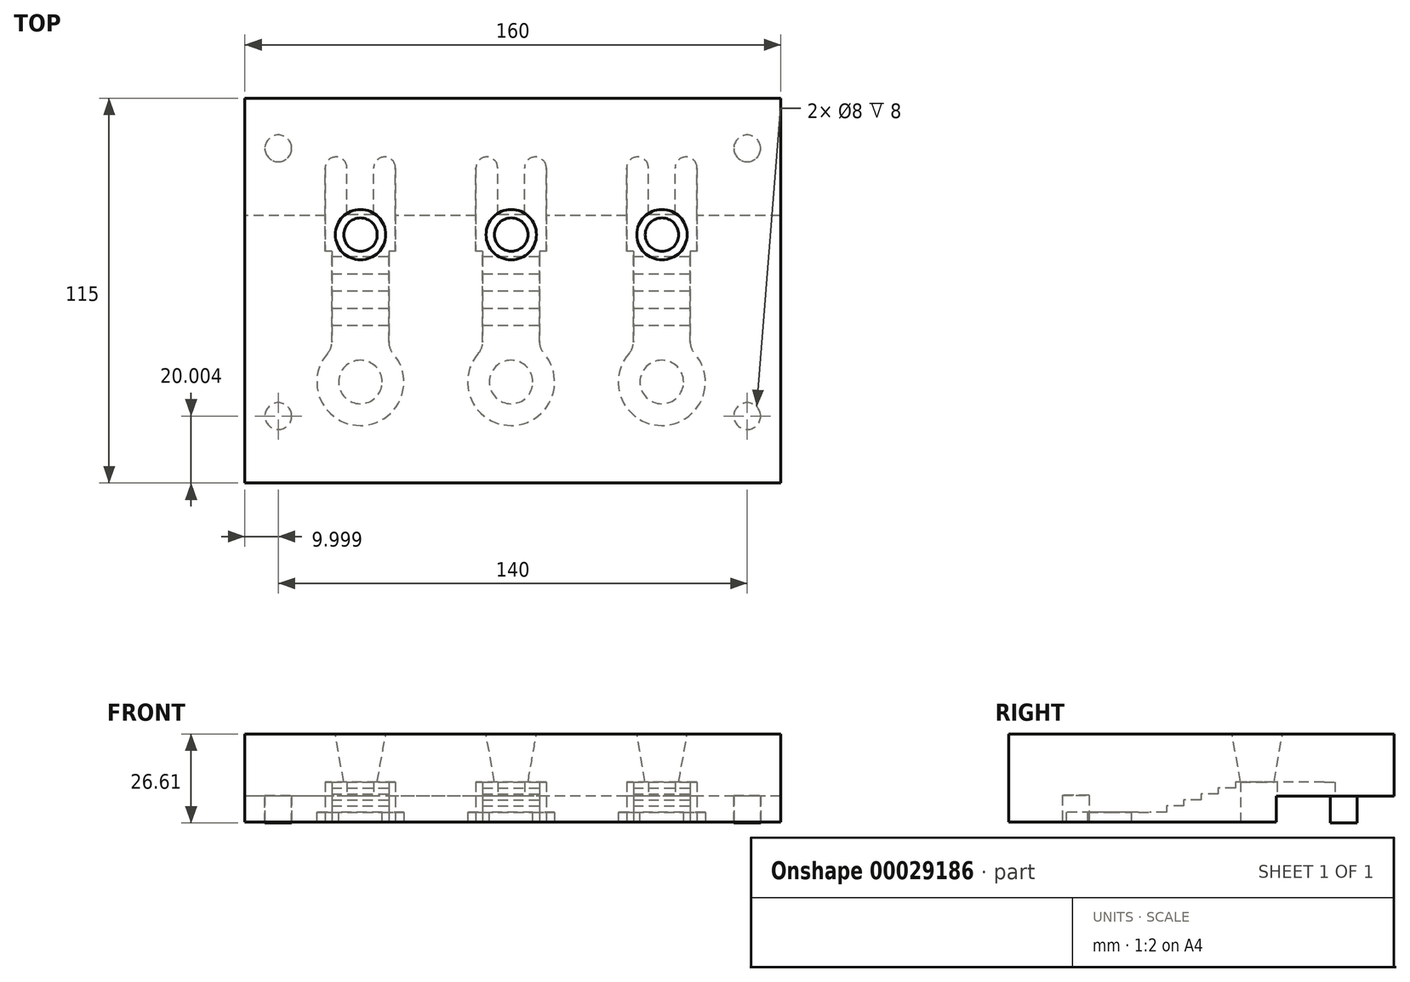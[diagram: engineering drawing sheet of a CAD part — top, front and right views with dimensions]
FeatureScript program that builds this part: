
annotation { "Feature Type Name" : "Feature", "Feature Type Description" : "" }
export const myFeature = defineFeature(function(context is Context, id is Id, definition is map)
    precondition{}
    {
        {
            var Q0;
            Q0=qCreatedBy(makeId("Top.planeOp"),FACE);
            var sketch = newSketch(context, id + "F0", { "sketchPlane" : qUnion([Q0])});
            skLineSegment(sketch, "E0.top", {"start": v(-85.13, 11.8) * mm, "end": v(-83.13, 11.8) * mm});
            skLineSegment(sketch, "E0.left", {"start": v(-85.13, 36.8) * mm, "end": v(-85.13, 11.8) * mm});
            skLineSegment(sketch, "E0.right", {"start": v(-64.13, 36.8) * mm, "end": v(-64.13, 11.8) * mm});
            skLineSegment(sketch, "E1.top", {"start": v(-78.63, 22.8) * mm, "end": v(-70.63, 22.8) * mm});
            skLineSegment(sketch, "E1.left", {"start": v(-78.63, 36.8) * mm, "end": v(-78.63, 22.8) * mm});
            skLineSegment(sketch, "E1.right", {"start": v(-70.63, 36.8) * mm, "end": v(-70.63, 22.8) * mm});
            skLineSegment(sketch, "E2.left", {"start": v(-83.13, 11.8) * mm, "end": v(-83.13, -15.3) * mm});
            skLineSegment(sketch, "E2.right", {"start": v(-66.13, 11.8) * mm, "end": v(-66.13, -15.3) * mm});
            skArc(sketch, "E3", {"start": v(-84.38, -18.6) * mm, "mid": v(-74.63, -40.2) * mm, "end": v(-64.88, -18.6) * mm});
            skLineSegment(sketch, "E4", {"start": v(-74.63, 22.8) * mm, "end": v(-74.63, -62.63) * mm, "construction": true});
            skPoint(sketch, "E5.visualSharp", {"position": v(-66.13, -17.37) * mm});
            skArc(sketch, "E5.filletArc", {"start": v(-66.13, -15.3) * mm, "mid": v(-65.8, -17.07) * mm, "end": v(-64.88, -18.6) * mm});
            skPoint(sketch, "E6.visualSharp", {"position": v(-83.13, -17.37) * mm});
            skArc(sketch, "E6.filletArc", {"start": v(-84.38, -18.6) * mm, "mid": v(-83.45, -17.07) * mm, "end": v(-83.13, -15.3) * mm});
            skPoint(sketch, "E7.visualSharp", {"position": v(-64.13, 11.8) * mm});
            skLineSegment(sketch, "E7.filletArc", {"start": v(-64.13, 11.8) * mm, "end": v(-64.13, 11.8) * mm});
            skPoint(sketch, "E8.visualSharp", {"position": v(-85.13, 11.8) * mm});
            skLineSegment(sketch, "E8.filletArc", {"start": v(-85.13, 11.8) * mm, "end": v(-85.13, 11.8) * mm});
            skLineSegment(sketch, "E9.trimOffspring", {"start": v(-66.13, 11.8) * mm, "end": v(-64.13, 11.8) * mm});
            skPoint(sketch, "E10.visualSharp", {"position": v(-83.13, 11.8) * mm});
            skLineSegment(sketch, "E10.filletArc", {"start": v(-83.13, 11.8) * mm, "end": v(-83.13, 11.8) * mm});
            skPoint(sketch, "E11.visualSharp", {"position": v(-66.13, 11.8) * mm});
            skLineSegment(sketch, "E11.filletArc", {"start": v(-66.13, 11.8) * mm, "end": v(-66.13, 11.8) * mm});
            skCircle(sketch, "E12", {"center": v(-74.63, -27.2) * mm, "radius": 6.5 * mm});
            skArc(sketch, "E13", {"start": v(-78.63, 36.8) * mm, "mid": v(-81.88, 40.05) * mm, "end": v(-85.13, 36.8) * mm});
            skArc(sketch, "E14", {"start": v(-64.13, 36.8) * mm, "mid": v(-67.38, 40.05) * mm, "end": v(-70.63, 36.8) * mm});
            skSolve(sketch);
        }
        {
            var Q0;
            Q0=makeQuery(id+"F0.imprint","IMPRINT",FACE,{"disambiguationData":[TD([[makeQuery(id+"F0.imprint","IMPRINT",EDGE,{"derivedFrom":sQuery(id+"F0.wireOp",EDGE,"E12")}),1.0]])]});
            var Q1;
            Q1=makeQuery(id+"F0.imprint","IMPRINT",FACE,{"disambiguationData":[TD([[makeQuery(id+"F0.imprint","IMPRINT",EDGE,{"derivedFrom":sQuery(id+"F0.wireOp",EDGE,"E0.top")}),1.0]])]});
            extrude(context, id + "F1", {"entities" : qUnion([Q0, Q1]), "depth" : 18 * mm});
        }
        {
            var Q0;
            Q0=qCreatedBy(makeId("Right.planeOp"),FACE);
            var sketch = newSketch(context, id + "F2", { "sketchPlane" : qUnion([Q0])});
            skLineSegment(sketch, "E15", {"start": v(-40.29, 25.83) * mm, "end": v(15.45, 25.83) * mm});
            skLineSegment(sketch, "E16", {"start": v(15.45, 25.83) * mm, "end": v(15.45, 18) * mm});
            skLineSegment(sketch, "E17", {"start": v(-10.3, 9) * mm, "end": v(-41.5, 9) * mm});
            skLineSegment(sketch, "E18", {"start": v(-41.5, 9) * mm, "end": v(-40.29, 25.83) * mm});
            skLineSegment(sketch, "E19", {"start": v(15.45, 18) * mm, "end": v(10.3, 18) * mm});
            skLineSegment(sketch, "E20", {"start": v(10.3, 18) * mm, "end": v(10.3, 16.2) * mm});
            skLineSegment(sketch, "E21", {"start": v(10.3, 16.2) * mm, "end": v(5.15, 16.2) * mm});
            skLineSegment(sketch, "E22", {"start": v(5.15, 16.2) * mm, "end": v(5.15, 14.4) * mm});
            skLineSegment(sketch, "E23", {"start": v(5.15, 14.4) * mm, "end": v(0, 14.4) * mm});
            skLineSegment(sketch, "E24", {"start": v(0, 14.4) * mm, "end": v(0, 12.6) * mm});
            skLineSegment(sketch, "E25", {"start": v(0, 12.6) * mm, "end": v(-5.15, 12.6) * mm});
            skLineSegment(sketch, "E26", {"start": v(-5.15, 12.6) * mm, "end": v(-5.15, 10.8) * mm});
            skLineSegment(sketch, "E27", {"start": v(-5.15, 10.8) * mm, "end": v(-10.3, 10.8) * mm});
            skLineSegment(sketch, "E28", {"start": v(-10.3, 10.8) * mm, "end": v(-10.3, 9) * mm});
            skSolve(sketch);
        }
        {
            var Q0;
            Q0=qSketchRegion(id+"F2",true);
            extrude(context, id + "F3", {"entities" : qUnion([Q0]), "operationType" : NewBodyOperationType.REMOVE, "oppositeDirection" : true, "depth" : 125 * mm});
        }
        {
            var Q0;
            Q0=makeQuery(id+"F3.boolean.opBoolean","COPY",FACE,{"derivedFrom":makeQuery(id+"F3.opExtrude","SWEPT_FACE",FACE,{"disambiguationData":[OSD([sQuery(id+"F2.wireOp",EDGE,"E17")])]})});
            var sketch = newSketch(context, id + "F4", { "sketchPlane" : qUnion([Q0])});
            skCircle(sketch, "E29", {"center": v(-74.63, -27.2) * mm, "radius": 6.5 * mm});
            skSolve(sketch);
        }
        {
            var Q0;
            Q0=qSketchRegion(id+"F4",true);
            extrude(context, id + "F5", {"entities" : qUnion([Q0]), "operationType" : NewBodyOperationType.REMOVE, "oppositeDirection" : true, "depth" : 3 * mm});
        }
        {
            var Q0;
            Q0=makeQuery(id+"F1.opExtrude","SWEPT_FACE",FACE,{"disambiguationData":[OSD([sQuery(id+"F0.wireOp",EDGE,"E0.right")])]});
            var sketch = newSketch(context, id + "F6", { "sketchPlane" : qUnion([Q0])});
            skCircle(sketch, "E30", {"center": v(30.8, 6) * mm, "radius": 2.5 * mm});
            skSolve(sketch);
        }
        {
            var Q0;
            Q0=makeQuery(id+"F1.opExtrude","SWEPT_FACE",FACE,{"disambiguationData":[OSD([sQuery(id+"F0.wireOp",EDGE,"E0.right")])]});
            var sketch = newSketch(context, id + "F7", { "sketchPlane" : qUnion([Q0])});
            skLineSegment(sketch, "E31", {"start": v(22.77, 0) * mm, "end": v(12.77, 0) * mm, "construction": true});
            skLineSegment(sketch, "E32", {"start": v(22.77, 0) * mm, "end": v(22.77, 17.98) * mm, "construction": true});
            skLineSegment(sketch, "E33", {"start": v(22.77, 17.98) * mm, "end": v(15.77, 17.98) * mm, "construction": true});
            skLineSegment(sketch, "E34", {"start": v(9.68, 20.3) * mm, "end": v(9.22, -2.99) * mm});
            skLineSegment(sketch, "E35", {"start": v(9.22, -2.99) * mm, "end": v(12.1, -2.99) * mm});
            skLineSegment(sketch, "E36", {"start": v(12.1, -2.99) * mm, "end": v(12.77, 0) * mm});
            skLineSegment(sketch, "E37", {"start": v(9.68, 20.3) * mm, "end": v(16.08, 19.87) * mm});
            skLineSegment(sketch, "E38", {"start": v(12.77, 0) * mm, "end": v(16.08, 19.87) * mm});
            skSolve(sketch);
        }
        {
            var Q0;
            Q0=makeQuery(id+"F1.opExtrude","SWEPT_FACE",FACE,{"disambiguationData":[OSD([sQuery(id+"F0.wireOp",EDGE,"E0.left")])]});
            var sketch = newSketch(context, id + "F8", { "sketchPlane" : qUnion([Q0])});
            skLineSegment(sketch, "E39", {"start": v(-12.8, 0) * mm, "end": v(-15.71, 18) * mm});
            skLineSegment(sketch, "E40", {"start": v(-15.71, 18) * mm, "end": v(-12.42, 21.29) * mm});
            skLineSegment(sketch, "E41", {"start": v(-12.42, 21.29) * mm, "end": v(-9.36, 20.22) * mm});
            skLineSegment(sketch, "E42", {"start": v(-9.36, 20.22) * mm, "end": v(-8.88, -2.86) * mm});
            skLineSegment(sketch, "E43", {"start": v(-8.88, -2.86) * mm, "end": v(-12.32, -2.93) * mm});
            skLineSegment(sketch, "E44", {"start": v(-12.32, -2.93) * mm, "end": v(-12.8, 0) * mm});
            skSolve(sketch);
        }
        {
            var Q0;
            Q0=makeQuery(id+"F1.opExtrude","SWEPT_FACE",FACE,{"disambiguationData":[OSD([sQuery(id+"F0.wireOp",EDGE,"E0.right")])]});
            var sketch = newSketch(context, id + "F9", { "sketchPlane" : qUnion([Q0])});
            skLineSegment(sketch, "E45", {"start": v(-57.39, 6) * mm, "end": v(-57.39, 32.33) * mm});
            skLineSegment(sketch, "E46", {"start": v(-57.39, 32.33) * mm, "end": v(57.61, 32.33) * mm});
            skLineSegment(sketch, "E47", {"start": v(57.61, 32.33) * mm, "end": v(57.61, 13.72) * mm});
            skLineSegment(sketch, "E48", {"start": v(57.61, 13.72) * mm, "end": v(57.61, -16.86) * mm});
            skLineSegment(sketch, "E49", {"start": v(57.61, -16.86) * mm, "end": v(-57.39, -16.86) * mm});
            skLineSegment(sketch, "E50", {"start": v(-57.39, -16.86) * mm, "end": v(-57.39, 6) * mm});
            skLineSegment(sketch, "E51", {"start": v(-57.39, 6) * mm, "end": v(22.49, 6) * mm});
            skLineSegment(sketch, "E52", {"start": v(22.49, 13.72) * mm, "end": v(22.49, 6) * mm});
            skLineSegment(sketch, "E53", {"start": v(22.49, 13.72) * mm, "end": v(57.61, 13.72) * mm});
            skSolve(sketch);
        }
        {
            var Q0;
            Q0=makeQuery(id+"F1.opExtrude","CAP_FACE",FACE,{"disambiguationData":[OSD([sQuery(id+"F0.wireOp",EDGE,"E0.top"),sQuery(id+"F0.wireOp",EDGE,"E0.left"),sQuery(id+"F0.wireOp",EDGE,"E0.right"),sQuery(id+"F0.wireOp",EDGE,"E1.top"),sQuery(id+"F0.wireOp",EDGE,"E1.left"),sQuery(id+"F0.wireOp",EDGE,"E1.right"),sQuery(id+"F0.wireOp",EDGE,"E2.left"),sQuery(id+"F0.wireOp",EDGE,"E2.right"),sQuery(id+"F0.wireOp",EDGE,"E3"),sQuery(id+"F0.wireOp",EDGE,"E5.filletArc"),sQuery(id+"F0.wireOp",EDGE,"E6.filletArc"),sQuery(id+"F0.wireOp",EDGE,"E9.trimOffspring"),sQuery(id+"F0.wireOp",EDGE,"E13"),sQuery(id+"F0.wireOp",EDGE,"E14")])],"isStart":false});
            var sketch = newSketch(context, id + "F10", { "sketchPlane" : qUnion([Q0])});
            skCircle(sketch, "E54", {"center": v(-74.58, 16.83) * mm, "radius": 5 * mm});
            skSolve(sketch);
        }
        {
            var Q0;
            Q0=qSketchRegion(id+"F10",true);
            extrude(context, id + "F11", {"entities" : qUnion([Q0]), "operationType" : NewBodyOperationType.ADD, "depth" : 25 * mm, "hasDraft" : true, "draftAngle" : 10 * degree});
        }
        {
            var Q0;
            {var subQ8=sQuery(id+"F9.wireOp",EDGE,"E52");Q0=makeQuery(id+"F9.imprint","IMPRINT",FACE,{"disambiguationData":[TD([[makeQuery(id+"F9.imprint","IMPRINT",EDGE,{"derivedFrom":subQ8}),-1.0]])]});}
            var Q1;
            {var subQ9=sQuery(id+"F9.wireOp",EDGE,"E45");Q1=makeQuery(id+"F9.imprint","IMPRINT",FACE,{"disambiguationData":[TD([[makeQuery(id+"F9.imprint","IMPRINT",EDGE,{"derivedFrom":subQ9}),-1.0]])]});}
            extrude(context, id + "F12", {"entities" : qUnion([Q0, Q1]), "depth" : 70 * mm, "hasSecondDirection" : true, "secondDirectionOppositeDirection" : true, "secondDirectionDepth" : 90 * mm});
        }
        {
            var Q0;
            Q0=makeQuery(id+"F12.opExtrude","SWEPT_FACE",FACE,{"disambiguationData":[OSD([sQuery(id+"F9.wireOp",EDGE,"E51")])]});
            var sketch = newSketch(context, id + "F13", { "sketchPlane" : qUnion([Q0])});
            skCircle(sketch, "E55", {"center": v(-144.13, 37.39) * mm, "radius": 4 * mm});
            skCircle(sketch, "E56", {"center": v(-4.13, 37.39) * mm, "radius": 4 * mm});
            skLineSegment(sketch, "E57", {"start": v(-144.13, 37.39) * mm, "end": v(-4.13, 37.39) * mm, "construction": true});
            skSolve(sketch);
        }
        {
            var Q0;
            Q0=makeQuery(id+"F12.opExtrude","SWEPT_FACE",FACE,{"disambiguationData":[OSD([sQuery(id+"F9.wireOp",EDGE,"E53")])]});
            var sketch = newSketch(context, id + "F14", { "sketchPlane" : qUnion([Q0])});
            skCircle(sketch, "E58", {"center": v(-144.13, -42.61) * mm, "radius": 4 * mm});
            skCircle(sketch, "E59", {"center": v(-4.13, -42.61) * mm, "radius": 4 * mm});
            skLineSegment(sketch, "E60", {"start": v(-144.13, -42.61) * mm, "end": v(-4.13, -42.61) * mm, "construction": true});
            skSolve(sketch);
        }
        {
            var Q0;
            Q0=makeQuery(id+"F14.imprint","IMPRINT",FACE,{"disambiguationData":[TD([[makeQuery(id+"F14.imprint","IMPRINT",EDGE,{"derivedFrom":sQuery(id+"F14.wireOp",EDGE,"E58")}),1.0]])]});
            var Q1;
            Q1=makeQuery(id+"F14.imprint","IMPRINT",FACE,{"disambiguationData":[TD([[makeQuery(id+"F14.imprint","IMPRINT",EDGE,{"derivedFrom":sQuery(id+"F14.wireOp",EDGE,"E59")}),1.0]])]});
            extrude(context, id + "F15", {"entities" : qUnion([Q0, Q1]), "operationType" : NewBodyOperationType.ADD, "depth" : 8 * mm});
        }
        {
            var Q0;
            Q0=makeQuery(id+"F13.imprint","IMPRINT",FACE,{"disambiguationData":[TD([[makeQuery(id+"F13.imprint","IMPRINT",EDGE,{"derivedFrom":sQuery(id+"F13.wireOp",EDGE,"E55")}),1.0]])]});
            var Q1;
            Q1=makeQuery(id+"F13.imprint","IMPRINT",FACE,{"disambiguationData":[TD([[makeQuery(id+"F13.imprint","IMPRINT",EDGE,{"derivedFrom":sQuery(id+"F13.wireOp",EDGE,"E56")}),1.0]])]});
            extrude(context, id + "F16", {"entities" : qUnion([Q0, Q1]), "operationType" : NewBodyOperationType.REMOVE, "oppositeDirection" : true, "depth" : 8 * mm});
        }
        {
            var Q0;
            Q0=makeQuery(id+"F1.opExtrude","SWEPT_BODY",BODY,{"disambiguationData":[OSD([sQuery(id+"F0.wireOp",EDGE,"E0.top"),sQuery(id+"F0.wireOp",EDGE,"E0.left"),sQuery(id+"F0.wireOp",EDGE,"E0.right"),sQuery(id+"F0.wireOp",EDGE,"E1.top"),sQuery(id+"F0.wireOp",EDGE,"E1.left"),sQuery(id+"F0.wireOp",EDGE,"E1.right"),sQuery(id+"F0.wireOp",EDGE,"E2.left"),sQuery(id+"F0.wireOp",EDGE,"E2.right"),sQuery(id+"F0.wireOp",EDGE,"E3"),sQuery(id+"F0.wireOp",EDGE,"E5.filletArc"),sQuery(id+"F0.wireOp",EDGE,"E6.filletArc"),sQuery(id+"F0.wireOp",EDGE,"E9.trimOffspring"),sQuery(id+"F0.wireOp",EDGE,"E13"),sQuery(id+"F0.wireOp",EDGE,"E14")])]});
            transform(context, id + "F17", {"entities" : qUnion([Q0]), "transformType" : TransformType.TRANSLATION_3D, "dx" : 45 * mm, "dy" : 0 * mm, "dz" : 0 * mm, "makeCopy" : true});
        }
        {
            var Q0;
            Q0=makeQuery(id+"F1.opExtrude","SWEPT_BODY",BODY,{"disambiguationData":[OSD([sQuery(id+"F0.wireOp",EDGE,"E0.top"),sQuery(id+"F0.wireOp",EDGE,"E0.left"),sQuery(id+"F0.wireOp",EDGE,"E0.right"),sQuery(id+"F0.wireOp",EDGE,"E1.top"),sQuery(id+"F0.wireOp",EDGE,"E1.left"),sQuery(id+"F0.wireOp",EDGE,"E1.right"),sQuery(id+"F0.wireOp",EDGE,"E2.left"),sQuery(id+"F0.wireOp",EDGE,"E2.right"),sQuery(id+"F0.wireOp",EDGE,"E3"),sQuery(id+"F0.wireOp",EDGE,"E5.filletArc"),sQuery(id+"F0.wireOp",EDGE,"E6.filletArc"),sQuery(id+"F0.wireOp",EDGE,"E9.trimOffspring"),sQuery(id+"F0.wireOp",EDGE,"E13"),sQuery(id+"F0.wireOp",EDGE,"E14")])]});
            transform(context, id + "F18", {"entities" : qUnion([Q0]), "transformType" : TransformType.TRANSLATION_3D, "dx" : -45 * mm, "dy" : 0 * mm, "dz" : 0 * mm, "makeCopy" : true});
        }
        {
            var Q0;
            Q0=makeQuery(id+"F1.opExtrude","SWEPT_BODY",BODY,{"disambiguationData":[OSD([sQuery(id+"F0.wireOp",EDGE,"E0.bottom"),sQuery(id+"F0.wireOp",EDGE,"E0.top"),sQuery(id+"F0.wireOp",EDGE,"E0.left"),sQuery(id+"F0.wireOp",EDGE,"E0.right"),sQuery(id+"F0.wireOp",EDGE,"E1.top"),sQuery(id+"F0.wireOp",EDGE,"E1.left"),sQuery(id+"F0.wireOp",EDGE,"E1.right"),sQuery(id+"F0.wireOp",EDGE,"3b6ef628-da63-4f4e-a1c5-ea05c0a2540d.trimOffspring"),sQuery(id+"F0.wireOp",EDGE,"E2.left"),sQuery(id+"F0.wireOp",EDGE,"E2.right"),sQuery(id+"F0.wireOp",EDGE,"E3"),sQuery(id+"F0.wireOp",EDGE,"E5.filletArc"),sQuery(id+"F0.wireOp",EDGE,"E6.filletArc"),sQuery(id+"F0.wireOp",EDGE,"E9.trimOffspring")])]});
            var Q1;
            Q1=makeQuery(id+"F18.opPattern","COPY",BODY,{"derivedFrom":makeQuery(id+"F1.opExtrude","SWEPT_BODY",BODY,{"disambiguationData":[OSD([sQuery(id+"F0.wireOp",EDGE,"E0.top"),sQuery(id+"F0.wireOp",EDGE,"E0.left"),sQuery(id+"F0.wireOp",EDGE,"E0.right"),sQuery(id+"F0.wireOp",EDGE,"E1.top"),sQuery(id+"F0.wireOp",EDGE,"E1.left"),sQuery(id+"F0.wireOp",EDGE,"E1.right"),sQuery(id+"F0.wireOp",EDGE,"E2.left"),sQuery(id+"F0.wireOp",EDGE,"E2.right"),sQuery(id+"F0.wireOp",EDGE,"E3"),sQuery(id+"F0.wireOp",EDGE,"E5.filletArc"),sQuery(id+"F0.wireOp",EDGE,"E6.filletArc"),sQuery(id+"F0.wireOp",EDGE,"E9.trimOffspring"),sQuery(id+"F0.wireOp",EDGE,"E13"),sQuery(id+"F0.wireOp",EDGE,"E14")])]}),"instanceName":"1"});
            var Q2;
            Q2=makeQuery(id+"F17.opPattern","COPY",BODY,{"derivedFrom":makeQuery(id+"F1.opExtrude","SWEPT_BODY",BODY,{"disambiguationData":[OSD([sQuery(id+"F0.wireOp",EDGE,"E0.top"),sQuery(id+"F0.wireOp",EDGE,"E0.left"),sQuery(id+"F0.wireOp",EDGE,"E0.right"),sQuery(id+"F0.wireOp",EDGE,"E1.top"),sQuery(id+"F0.wireOp",EDGE,"E1.left"),sQuery(id+"F0.wireOp",EDGE,"E1.right"),sQuery(id+"F0.wireOp",EDGE,"E2.left"),sQuery(id+"F0.wireOp",EDGE,"E2.right"),sQuery(id+"F0.wireOp",EDGE,"E3"),sQuery(id+"F0.wireOp",EDGE,"E5.filletArc"),sQuery(id+"F0.wireOp",EDGE,"E6.filletArc"),sQuery(id+"F0.wireOp",EDGE,"E9.trimOffspring"),sQuery(id+"F0.wireOp",EDGE,"E13"),sQuery(id+"F0.wireOp",EDGE,"E14")])]}),"instanceName":"1"});
            var Q3;
            Q3=makeQuery(id+"F12.opExtrude","SWEPT_BODY",BODY,{"disambiguationData":[OSD([sQuery(id+"F9.wireOp",EDGE,"a7e27d74-994a-4891-aaa3-0980bfbdc30e"),sQuery(id+"F9.wireOp",EDGE,"fb911d7a-c046-4048-9a62-8b9bea53e43f"),sQuery(id+"F9.wireOp",EDGE,"E45"),sQuery(id+"F9.wireOp",EDGE,"E46"),sQuery(id+"F9.wireOp",EDGE,"E47"),sQuery(id+"F9.wireOp",EDGE,"ea3ffea4-3806-48fb-9a5a-532117da88c0")])]});
            var Q4;
            Q4=makeQuery(id+"F12.opExtrude","SWEPT_BODY",BODY,{"disambiguationData":[OSD([sQuery(id+"F9.wireOp",EDGE,"E48"),sQuery(id+"F9.wireOp",EDGE,"E49"),sQuery(id+"F9.wireOp",EDGE,"E50"),sQuery(id+"F9.wireOp",EDGE,"E51"),sQuery(id+"F9.wireOp",EDGE,"E52"),sQuery(id+"F9.wireOp",EDGE,"E53")])]});
            booleanBodies(context, id + "F19", {"operationType" : BooleanOperationType.SUBTRACTION, "tools" : qUnion([Q0, Q1, Q2]), "targets" : qUnion([Q3, Q4])});
        }
    });
